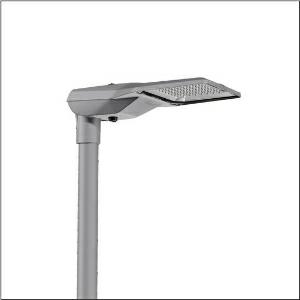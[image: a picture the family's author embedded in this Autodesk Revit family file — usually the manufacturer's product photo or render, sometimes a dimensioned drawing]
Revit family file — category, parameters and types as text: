
# Revit family: streetlight_sl_21_midi___pc-r_5xe3g33t08mb_dbe8
name_source: partatom
category: Lighting Fixtures
units: mm (PartAtom-declared; Revit-internal decimal feet)

## family parameters
Cut with Voids When Loaded = No
Host = Face
Light Source = No
Part Type = Normal
Room Calculation Point = No
Round Connector Dimension = Use Diameter
Shared = No

## types (1)
- --- (1 x LED, 17390 lm, 136 W, 3000K)
    Apparent Load = 136 VA
    CIE Flux Codes = 38 78 98 100 100
    Color Rendering = 70
    Color Temperature = 3000K
    Default Elevation = 1800 mm
    Description = Streetlight SL 21 midi, mast luminaire, primary light control with lens, of PMMA, primary optical cover: cover, of toughened safety glass, transparent, light distribution: PC-R, light emission: direct distribution, primary light characteristic: asymmetric, right, installation type: side-entry, post-top, LED, High Power LED, rated luminous flux: 17.390lm, luminous efficacy: 128lm/W, light colour: 730, colour temperature: 3000K, control gear: D4i, control: overheat protection, constant luminous flux control, time-dependent luminous flux control, flexible luminous flux parameterisation, pre-setting: logarithmic dimming characteristic, mains connection: 230..240V, AC, 50/60Hz, start of lifetime: 136W, end of service life: 142W, reduction: 61W, luminaire housing, of diecast aluminium, powder-coated, Siteco® metallic grey (DB 702S), corrosivity category C5 mid according to DIN EN ISO 12944, please order mast flange separately, inclination adjustable: 0°, 5°, 10°, 15°, sealing non-destructively replaceable, multi-level sealing system, length: 644mm, width: 335mm, height: 110mm, mast flange for spigot size: 42mm (side-entry): 5XC10008XM4, 60/48mm (side-entry/post-top): 5XC10108XM2, 76/60mm (side-entry/post-top): 5XC10108XM1, mounting height: 4..8m, Smart Interface below and above, protection rating (complete): IP66, insulation class (complete): insulation class II (safety insulation), certification: CE, ENEC, ENEC+, VDE, impact resistance: IK10, permissible operating ambient temperature for outdoor applications: -40..+50°C, standard-compliant lighting for roads and squares, packaging unit: 1 piece

Light Distribution: PC-R
    Height = 111 mm
    Lamp = 1 x LED
    Lamp Light Flux = 17390 lm
    Lamp Power = 136 W
    Lamp count = 1
    Length = 644 mm
    Luminous efficacy = 128 lm/W
    Manufacturer = Siteco
    ModVariant = No
    Model = 5XE3G33T08MB
    Number of Poles = 1
    OnlyDefault = Yes
    Power Factor = 1
    Product Name = Streetlight SL 21 midi | PC-R
    Product group = mast luminaire | pylon top
    ProductGroupID = 6100
    Protection Class = Protection class II
    Protection Degree = IP 66
    RLX_Detail_Level = 1
    RLX_Emergency_Light_Flux = 0 lm
    RLX_Emergency_Type = 0
    RLX_Emergency_Type_DB = No
    RlxData = <blob elided: 29497 chars, md5=bc58e94e>
    Socket = socket
    Standby Power = 0 W
    System Light Flux = 17390 lm
    System Power = 136 W
    Type Comments = factory setting: luminous flux: 100 % | dim-lin: 254 | 695 mA
    Type Image = l_1004304.jpg
    URL = http://relux.com
    VarID = @adj_085535
    Voltage = 0 V
    Weight = 0.00 kg
    Width = 336 mm

## geometry (parser evidence)
native form markers: Blend x4, Sweep x11
no freeform markers — native parametric forms only
